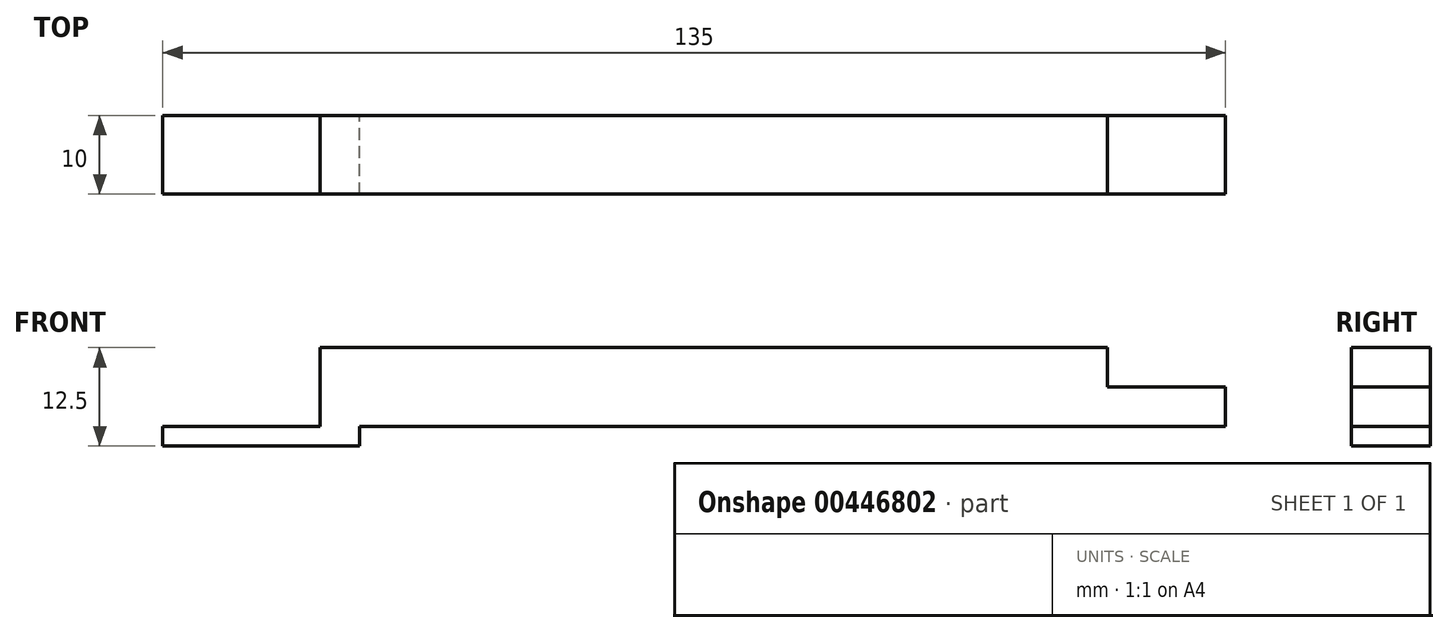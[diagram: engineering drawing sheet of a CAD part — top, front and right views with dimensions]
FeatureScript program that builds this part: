
annotation { "Feature Type Name" : "Feature", "Feature Type Description" : "" }
export const myFeature = defineFeature(function(context is Context, id is Id, definition is map)
    precondition{}
    {
        {
            var Q0;
            Q0=qCreatedBy(makeId("Front.planeOp"),FACE);
            var sketch = newSketch(context, id + "F0", { "sketchPlane" : qUnion([Q0])});
            skLineSegment(sketch, "E0.bottom", {"start": v(-57.5, 0) * mm, "end": v(57.5, 0) * mm});
            skLineSegment(sketch, "E0.top", {"start": v(-57.5, -10) * mm, "end": v(57.5, -10) * mm});
            skLineSegment(sketch, "E0.left", {"start": v(-57.5, 0) * mm, "end": v(-57.5, -10) * mm});
            skLineSegment(sketch, "E0.right", {"start": v(57.5, 0) * mm, "end": v(57.5, -10) * mm});
            skSolve(sketch);
        }
        {
            var Q0;
            Q0=qSketchRegion(id+"F0",true);
            extrude(context, id + "F1", {"entities" : qUnion([Q0]), "depth" : 10 * mm});
        }
        {
            var Q0;
            Q0=makeQuery(id+"F1.opExtrude","SWEPT_FACE",FACE,{"disambiguationData":[OSD([sQuery(id+"F0.wireOp",EDGE,"E0.bottom")])]});
            var sketch = newSketch(context, id + "F2", { "sketchPlane" : qUnion([Q0])});
            skLineSegment(sketch, "E1.bottom", {"start": v(42.5, 0) * mm, "end": v(57.5, 0) * mm});
            skLineSegment(sketch, "E1.top", {"start": v(42.5, -10) * mm, "end": v(57.5, -10) * mm});
            skLineSegment(sketch, "E1.left", {"start": v(42.5, 0) * mm, "end": v(42.5, -10) * mm});
            skLineSegment(sketch, "E1.right", {"start": v(57.5, 0) * mm, "end": v(57.5, -10) * mm});
            skSolve(sketch);
        }
        {
            var Q0;
            Q0=makeQuery(id+"F2.imprint","IMPRINT",FACE,{"disambiguationData":[TD([[makeQuery(id+"F2.imprint","IMPRINT",EDGE,{"derivedFrom":sQuery(id+"F2.wireOp",EDGE,"E1.bottom")}),-1.0]])]});
            extrude(context, id + "F3", {"entities" : qUnion([Q0]), "operationType" : NewBodyOperationType.REMOVE, "oppositeDirection" : true, "depth" : 5 * mm});
        }
        {
            var Q0;
            Q0=makeQuery(id+"F1.opExtrude","SWEPT_FACE",FACE,{"disambiguationData":[OSD([sQuery(id+"F0.wireOp",EDGE,"E0.top")])]});
            var sketch = newSketch(context, id + "F4", { "sketchPlane" : qUnion([Q0])});
            skLineSegment(sketch, "E2.bottom", {"start": v(-52.5, 10) * mm, "end": v(-77.5, 10) * mm});
            skLineSegment(sketch, "E2.top", {"start": v(-52.5, 0) * mm, "end": v(-77.5, 0) * mm});
            skLineSegment(sketch, "E2.left", {"start": v(-52.5, 10) * mm, "end": v(-52.5, 0) * mm});
            skLineSegment(sketch, "E2.right", {"start": v(-77.5, 10) * mm, "end": v(-77.5, 0) * mm});
            skSolve(sketch);
        }
        {
            var Q0;
            Q0=qSketchRegion(id+"F4",true);
            extrude(context, id + "F5", {"entities" : qUnion([Q0]), "operationType" : NewBodyOperationType.ADD, "depth" : 2.5 * mm});
        }
    });
